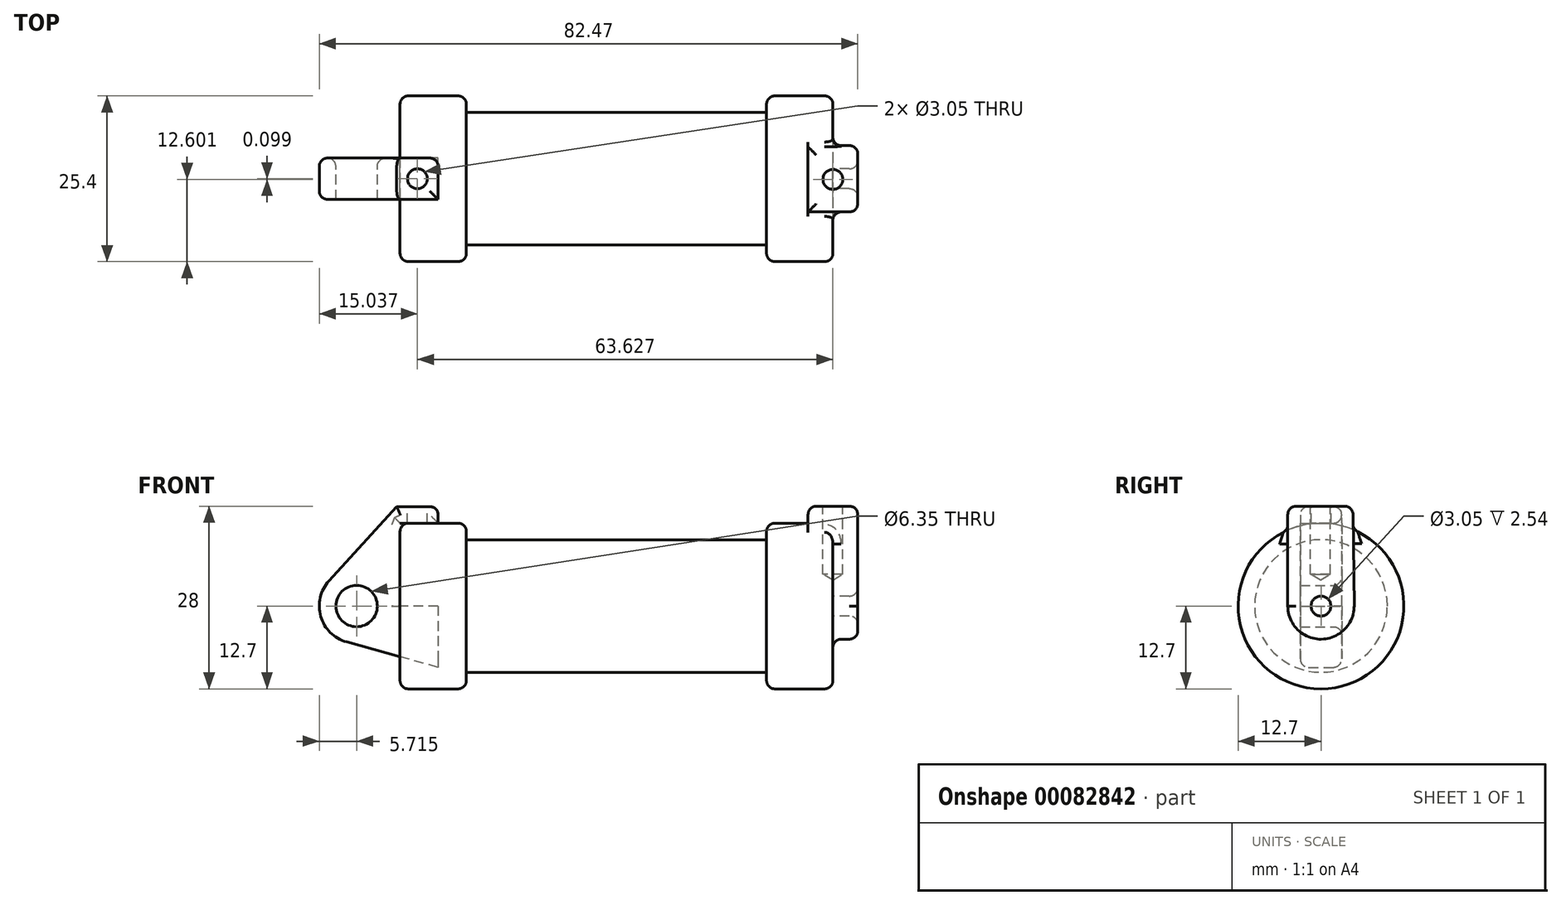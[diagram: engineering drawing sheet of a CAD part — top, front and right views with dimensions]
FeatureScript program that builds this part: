
annotation { "Feature Type Name" : "Feature", "Feature Type Description" : "" }
export const myFeature = defineFeature(function(context is Context, id is Id, definition is map)
    precondition{}
    {
        {
            var Q0;
            Q0=qCreatedBy(makeId("Front.planeOp"),FACE);
            var sketch = newSketch(context, id + "F0", { "sketchPlane" : qUnion([Q0])});
            skLineSegment(sketch, "E0", {"start": v(0, 0) * mm, "end": v(0, 12.7) * mm});
            skLineSegment(sketch, "E1", {"start": v(0, 12.7) * mm, "end": v(10.16, 12.7) * mm});
            skLineSegment(sketch, "E2", {"start": v(10.16, 12.7) * mm, "end": v(10.16, 10.16) * mm});
            skLineSegment(sketch, "E3", {"start": v(10.16, 10.16) * mm, "end": v(56.13, 10.16) * mm});
            skLineSegment(sketch, "E4", {"start": v(56.13, 10.16) * mm, "end": v(56.13, 12.7) * mm});
            skLineSegment(sketch, "E5", {"start": v(56.13, 12.7) * mm, "end": v(66.3, 12.7) * mm});
            skLineSegment(sketch, "E6", {"start": v(66.3, 12.7) * mm, "end": v(66.3, 0) * mm});
            skLineSegment(sketch, "E7", {"start": v(66.3, 0) * mm, "end": v(0, 0) * mm});
            skLineSegment(sketch, "E8", {"start": v(5.84, 15.24) * mm, "end": v(-0.5, 15.24) * mm});
            skLineSegment(sketch, "E9", {"start": v(-0.5, 15.24) * mm, "end": v(-10.88, 3.85) * mm});
            skLineSegment(sketch, "E10", {"start": v(0, 0) * mm, "end": v(-6.65, 0) * mm});
            skCircle(sketch, "E11", {"center": v(-6.65, 0) * mm, "radius": 5.72 * mm});
            skCircle(sketch, "E12", {"center": v(-6.65, 0) * mm, "radius": 3.18 * mm});
            skLineSegment(sketch, "E13", {"start": v(5.84, 15.24) * mm, "end": v(5.84, -9.4) * mm});
            skLineSegment(sketch, "E14", {"start": v(5.84, -9.4) * mm, "end": v(-8.18, -5.5) * mm});
            skSolve(sketch);
        }
        {
            var Q0;
            {var subQ0=sQuery(id+"F0.wireOp",EDGE,"E2");Q0=makeQuery(id+"F0.imprint","IMPRINT",FACE,{"disambiguationData":[TD([[makeQuery(id+"F0.imprint","IMPRINT",EDGE,{"derivedFrom":subQ0}),-1.0]])]});}
            var Q1;
            {var subQ0=sQuery(id+"F0.wireOp",EDGE,"E0");Q1=makeQuery(id+"F0.imprint","IMPRINT",FACE,{"disambiguationData":[TD([[makeQuery(id+"F0.imprint","IMPRINT",EDGE,{"derivedFrom":subQ0}),-1.0]])]});}
            var Q2;
            Q2=sQuery(id+"F0.wireOp",EDGE,"E7");
            revolve(context, id + "F1", {"entities" : qUnion([Q0, Q1]), "axis" : qUnion([Q2]), "revolveType" : RevolveType.FULL});
        }
        {
            var Q0;
            {var subQ3=sQuery(id+"F0.wireOp",EDGE,"E0");Q0=makeQuery(id+"F0.imprint","IMPRINT",FACE,{"disambiguationData":[TD([[makeQuery(id+"F0.imprint","IMPRINT",EDGE,{"derivedFrom":subQ3}),1.0]])]});}
            var Q1;
            {var subQ0=sQuery(id+"F0.wireOp",EDGE,"E14");Q1=makeQuery(id+"F0.imprint","IMPRINT",FACE,{"disambiguationData":[TD([[makeQuery(id+"F0.imprint","IMPRINT",EDGE,{"derivedFrom":subQ0}),-1.0]])]});}
            var Q2;
            {var subQ4=sQuery(id+"F0.wireOp",EDGE,"E12");Q2=makeQuery(id+"F0.imprint","IMPRINT",FACE,{"disambiguationData":[TD([[makeQuery(id+"F0.imprint","IMPRINT",EDGE,{"derivedFrom":subQ4}),-1.0]])]});}
            extrude(context, id + "F2", {"entities" : qUnion([Q0, Q1, Q2]), "endBound" : BoundingType.SYMMETRIC, "depth" : 6.35 * mm});
        }
        {
            var Q0;
            Q0=makeQuery(id+"F1.opRevolve","SWEPT_FACE",FACE,{"disambiguationData":[OSD([sQuery(id+"F0.wireOp",EDGE,"E6")])]});
            var sketch = newSketch(context, id + "F3", { "sketchPlane" : qUnion([Q0])});
            skCircle(sketch, "E15", {"center": v(0, 0) * mm, "radius": 1.52 * mm});
            skCircle(sketch, "E16", {"center": v(0, 0) * mm, "radius": 5.08 * mm});
            skLineSegment(sketch, "E17", {"start": v(-5.08, -0.04) * mm, "end": v(-5.08, 15.3) * mm});
            skLineSegment(sketch, "E18", {"start": v(-5.08, 15.3) * mm, "end": v(4.88, 15.3) * mm});
            skLineSegment(sketch, "E19", {"start": v(4.88, 15.3) * mm, "end": v(5.08, 0.07) * mm});
            skSolve(sketch);
        }
        {
            var Q0;
            {var subQ0=sQuery(id+"F3.wireOp",EDGE,"E19");var subQ1=sQuery(id+"F3.wireOp",EDGE,"E16");var subQ2=makeQuery(id+"F3.imprint","INTERSECT",VERTEX,{"derivedFrom":[subQ1,subQ0]});Q0=makeQuery(id+"F3.imprint","IMPRINT",FACE,{"disambiguationData":[TD([[makeQuery(id+"F3.imprint","IMPRINT",EDGE,{"disambiguationData":[TD([[subQ2,-1.0]])],"derivedFrom":subQ1}),-1.0]])]});}
            var Q1;
            {var subQ0=sQuery(id+"F3.wireOp",EDGE,"E18");Q1=makeQuery(id+"F3.imprint","IMPRINT",FACE,{"disambiguationData":[TD([[makeQuery(id+"F3.imprint","IMPRINT",EDGE,{"derivedFrom":subQ0}),-1.0]])]});}
            var Q2;
            Q2=makeQuery(id+"F3.imprint","IMPRINT",FACE,{"disambiguationData":[TD([[makeQuery(id+"F3.imprint","IMPRINT",EDGE,{"derivedFrom":sQuery(id+"F3.wireOp",EDGE,"E15")}),-1.0]])]});
            extrude(context, id + "F4", {"entities" : qUnion([Q0, Q1, Q2]), "operationType" : NewBodyOperationType.ADD, "endBound" : BoundingType.SYMMETRIC, "depth" : 7.62 * mm});
        }
        {
            var Q0;
            Q0=makeQuery(id+"F2.opExtrude","SWEPT_FACE",FACE,{"disambiguationData":[OSD([sQuery(id+"F0.wireOp",EDGE,"E8")])]});
            var sketch = newSketch(context, id + "F5", { "sketchPlane" : qUnion([Q0])});
            skLineSegment(sketch, "E20", {"start": v(-0.5, 3.18) * mm, "end": v(5.84, -3.18) * mm, "construction": true});
            skLineSegment(sketch, "E21", {"start": v(5.84, 3.18) * mm, "end": v(-0.5, -3.18) * mm, "construction": true});
            skCircle(sketch, "E22", {"center": v(2.67, 0) * mm, "radius": 1.52 * mm});
            skSolve(sketch);
        }
        {
            var Q0;
            Q0=makeQuery(id+"F4.opExtrude","SWEPT_FACE",FACE,{"disambiguationData":[OSD([sQuery(id+"F3.wireOp",EDGE,"E18")])]});
            var sketch = newSketch(context, id + "F6", { "sketchPlane" : qUnion([Q0])});
            skLineSegment(sketch, "E23", {"start": v(62.48, 4.88) * mm, "end": v(70.1, -5.08) * mm, "construction": true});
            skLineSegment(sketch, "E24", {"start": v(70.1, 4.88) * mm, "end": v(62.48, -5.08) * mm, "construction": true});
            skCircle(sketch, "E25", {"center": v(66.3, -0.1) * mm, "radius": 1.52 * mm});
            skSolve(sketch);
        }
        {
            var Q0;
            Q0=makeQuery(id+"F1.opRevolve","SWEPT_EDGE",EDGE,{"disambiguationData":[OSD([sQuery(id+"F0.wireOp",EDGE,"E1"),sQuery(id+"F0.wireOp",EDGE,"E2")])]});
            var Q1;
            Q1=makeQuery(id+"F1.opRevolve","SWEPT_EDGE",EDGE,{"disambiguationData":[OSD([sQuery(id+"F0.wireOp",EDGE,"E0"),sQuery(id+"F0.wireOp",EDGE,"E1")])]});
            fillet(context, id + "F7", {"entities" : qUnion([Q0, Q1]), "radius" : 1.27 * mm, "tangentPropagation" : true, "allowEdgeOverflow" : false});
        }
        {
            var Q0;
            Q0=makeQuery(id+"F1.opRevolve","SWEPT_EDGE",EDGE,{"disambiguationData":[OSD([sQuery(id+"F0.wireOp",EDGE,"E4"),sQuery(id+"F0.wireOp",EDGE,"E5")])]});
            var Q1;
            Q1=makeQuery(id+"F1.opRevolve","SWEPT_EDGE",EDGE,{"disambiguationData":[OSD([sQuery(id+"F0.wireOp",EDGE,"E5"),sQuery(id+"F0.wireOp",EDGE,"E6")])]});
            fillet(context, id + "F8", {"entities" : qUnion([Q0, Q1]), "radius" : 1.27 * mm, "tangentPropagation" : true, "allowEdgeOverflow" : false});
        }
        {
            var Q0;
            Q0=makeQuery(id+"F4.opExtrude","CAP_FACE",FACE,{"disambiguationData":[OSD([sQuery(id+"F3.wireOp",EDGE,"E15"),sQuery(id+"F3.wireOp",EDGE,"E16"),sQuery(id+"F3.wireOp",EDGE,"E17"),sQuery(id+"F3.wireOp",EDGE,"E18"),sQuery(id+"F3.wireOp",EDGE,"E19")])],"isStart":false});
            var Q1;
            Q1=makeQuery(id+"F4.opExtrude","SWEPT_EDGE",EDGE,{"disambiguationData":[OSD([sQuery(id+"F3.wireOp",EDGE,"E17"),sQuery(id+"F3.wireOp",EDGE,"E18")])]});
            var Q2;
            Q2=makeQuery(id+"F4.boolean.opBoolean","INTERSECT",EDGE,{"derivedFrom":[makeQuery(id+"F1.opRevolve","SWEPT_FACE",FACE,{"disambiguationData":[OSD([sQuery(id+"F0.wireOp",EDGE,"E6")])]}),makeQuery(id+"F4.opExtrude","SWEPT_FACE",FACE,{"disambiguationData":[OSD([sQuery(id+"F3.wireOp",EDGE,"E17")])]})]});
            var Q3;
            Q3=makeQuery(id+"F4.boolean.opBoolean","INTERSECT",EDGE,{"derivedFrom":[makeQuery(id+"F1.opRevolve","SWEPT_FACE",FACE,{"disambiguationData":[OSD([sQuery(id+"F0.wireOp",EDGE,"E5")])]}),makeQuery(id+"F4.opExtrude","SWEPT_FACE",FACE,{"disambiguationData":[OSD([sQuery(id+"F3.wireOp",EDGE,"E17")])]})]});
            var Q4;
            Q4=makeQuery(id+"F8.opFillet","BLEND_EDGE",EDGE,{"blendedFrom":[makeQuery(id+"F1.opRevolve","SWEPT_EDGE",EDGE,{"disambiguationData":[OSD([sQuery(id+"F0.wireOp",EDGE,"E5"),sQuery(id+"F0.wireOp",EDGE,"E6")])]}),makeQuery(id+"F4.opExtrude","SWEPT_FACE",FACE,{"disambiguationData":[OSD([sQuery(id+"F3.wireOp",EDGE,"E17")])]})],"blendedInto":[makeQuery(id+"F4.opExtrude","SWEPT_FACE",FACE,{"disambiguationData":[OSD([sQuery(id+"F3.wireOp",EDGE,"E17")])]})]});
            var Q5;
            Q5=makeQuery(id+"F4.boolean.opBoolean","INTERSECT",EDGE,{"derivedFrom":[makeQuery(id+"F1.opRevolve","SWEPT_FACE",FACE,{"disambiguationData":[OSD([sQuery(id+"F0.wireOp",EDGE,"E6")])]}),makeQuery(id+"F4.opExtrude","SWEPT_FACE",FACE,{"disambiguationData":[OSD([sQuery(id+"F3.wireOp",EDGE,"E16")])]})]});
            var Q6;
            Q6=makeQuery(id+"F4.opExtrude","CAP_EDGE",EDGE,{"disambiguationData":[OSD([sQuery(id+"F3.wireOp",EDGE,"E16")])],"isStart":false});
            var Q7;
            Q7=makeQuery(id+"F4.opExtrude","CAP_EDGE",EDGE,{"disambiguationData":[OSD([sQuery(id+"F3.wireOp",EDGE,"E17")])],"isStart":false});
            var Q8;
            {var subQ0=sQuery(id+"F0.wireOp",EDGE,"E5");var subQ1=sQuery(id+"F0.wireOp",EDGE,"E6");Q8=makeQuery(id+"F8.opFillet","BLEND_EDGE",EDGE,{"blendedFrom":[makeQuery(id+"F1.opRevolve","SWEPT_EDGE",EDGE,{"disambiguationData":[OSD([subQ0,subQ1])]}),makeQuery(id+"F4.boolean.opBoolean","SPLIT",FACE,{"disambiguationData":[TD([makeQuery(id+"F1.opRevolve","SWEPT_FACE",FACE,{"disambiguationData":[OSD([subQ0])]})])],"derivedFrom":makeQuery(id+"F1.opRevolve","SWEPT_FACE",FACE,{"disambiguationData":[OSD([subQ1])]})})],"blendedInto":[makeQuery(id+"F4.boolean.opBoolean","SPLIT",FACE,{"disambiguationData":[TD([makeQuery(id+"F1.opRevolve","SWEPT_FACE",FACE,{"disambiguationData":[OSD([subQ0])]})])],"derivedFrom":makeQuery(id+"F1.opRevolve","SWEPT_FACE",FACE,{"disambiguationData":[OSD([subQ1])]})})]});}
            var Q9;
            Q9=makeQuery(id+"F4.opExtrude","CAP_EDGE",EDGE,{"disambiguationData":[OSD([sQuery(id+"F3.wireOp",EDGE,"E18")])],"isStart":false});
            var Q10;
            Q10=makeQuery(id+"F4.opExtrude","SWEPT_EDGE",EDGE,{"disambiguationData":[OSD([sQuery(id+"F3.wireOp",EDGE,"E18"),sQuery(id+"F3.wireOp",EDGE,"E19")])]});
            var Q11;
            Q11=makeQuery(id+"F4.opExtrude","CAP_EDGE",EDGE,{"disambiguationData":[OSD([sQuery(id+"F3.wireOp",EDGE,"E18")])],"isStart":true});
            var Q12;
            Q12=makeQuery(id+"F4.opExtrude","CAP_EDGE",EDGE,{"disambiguationData":[OSD([sQuery(id+"F3.wireOp",EDGE,"E19")])],"isStart":false});
            var Q13;
            Q13=makeQuery(id+"F4.boolean.opBoolean","SPLIT",FACE,{"disambiguationData":[TD([makeQuery(id+"F1.opRevolve","SWEPT_FACE",FACE,{"disambiguationData":[OSD([sQuery(id+"F0.wireOp",EDGE,"E5")])]})])],"derivedFrom":makeQuery(id+"F1.opRevolve","SWEPT_FACE",FACE,{"disambiguationData":[OSD([sQuery(id+"F0.wireOp",EDGE,"E6")])]})});
            var Q14;
            Q14=makeQuery(id+"F8.opFillet","BLEND_EDGE",EDGE,{"blendedFrom":[makeQuery(id+"F1.opRevolve","SWEPT_EDGE",EDGE,{"disambiguationData":[OSD([sQuery(id+"F0.wireOp",EDGE,"E5"),sQuery(id+"F0.wireOp",EDGE,"E6")])]}),makeQuery(id+"F4.opExtrude","SWEPT_FACE",FACE,{"disambiguationData":[OSD([sQuery(id+"F3.wireOp",EDGE,"E19")])]})],"blendedInto":[makeQuery(id+"F4.opExtrude","SWEPT_FACE",FACE,{"disambiguationData":[OSD([sQuery(id+"F3.wireOp",EDGE,"E19")])]})]});
            var Q15;
            Q15=makeQuery(id+"F4.boolean.opBoolean","INTERSECT",EDGE,{"derivedFrom":[makeQuery(id+"F1.opRevolve","SWEPT_FACE",FACE,{"disambiguationData":[OSD([sQuery(id+"F0.wireOp",EDGE,"E5")])]}),makeQuery(id+"F4.opExtrude","SWEPT_FACE",FACE,{"disambiguationData":[OSD([sQuery(id+"F3.wireOp",EDGE,"E19")])]})]});
            fillet(context, id + "F9", {"entities" : qUnion([Q0, Q1, Q2, Q3, Q4, Q5, Q6, Q7, Q8, Q9, Q10, Q11, Q12, Q13, Q14, Q15]), "radius" : 1.27 * mm, "tangentPropagation" : true, "allowEdgeOverflow" : false});
        }
        {
            var Q0;
            Q0=makeQuery(id+"F2.opExtrude","CAP_EDGE",EDGE,{"disambiguationData":[OSD([sQuery(id+"F0.wireOp",EDGE,"E14")])],"isStart":true});
            var Q1;
            Q1=makeQuery(id+"F2.opExtrude","CAP_EDGE",EDGE,{"disambiguationData":[OSD([sQuery(id+"F0.wireOp",EDGE,"E14")])],"isStart":false});
            var Q2;
            Q2=makeQuery(id+"F2.opExtrude","CAP_EDGE",EDGE,{"disambiguationData":[OSD([sQuery(id+"F0.wireOp",EDGE,"E11")])],"isStart":false});
            var Q3;
            Q3=makeQuery(id+"F2.opExtrude","CAP_EDGE",EDGE,{"disambiguationData":[OSD([sQuery(id+"F0.wireOp",EDGE,"E11")])],"isStart":true});
            var Q4;
            Q4=makeQuery(id+"F2.opExtrude","CAP_EDGE",EDGE,{"disambiguationData":[OSD([sQuery(id+"F0.wireOp",EDGE,"E9")])],"isStart":true});
            var Q5;
            Q5=makeQuery(id+"F2.opExtrude","CAP_EDGE",EDGE,{"disambiguationData":[OSD([sQuery(id+"F0.wireOp",EDGE,"E9")])],"isStart":false});
            var Q6;
            Q6=makeQuery(id+"F2.opExtrude","CAP_EDGE",EDGE,{"disambiguationData":[OSD([sQuery(id+"F0.wireOp",EDGE,"E8")])],"isStart":false});
            var Q7;
            Q7=makeQuery(id+"FPSyX7AReI34fN4_2.hole-0.boolean.opBoolean","COPY",EDGE,{"derivedFrom":makeQuery(id+"FPSyX7AReI34fN4_2.hole-0.opRevolve","SWEPT_EDGE",EDGE,{"disambiguationData":[OSD([sQuery(id+"FPSyX7AReI34fN4_2.hole-0.sketch.wireOp",EDGE,"core_line_2"),sQuery(id+"FPSyX7AReI34fN4_2.hole-0.sketch.wireOp",EDGE,"core_line_3")])]})});
            var Q8;
            Q8=makeQuery(id+"F2.opExtrude","CAP_EDGE",EDGE,{"disambiguationData":[OSD([sQuery(id+"F0.wireOp",EDGE,"E8")])],"isStart":true});
            var Q9;
            Q9=makeQuery(id+"F2.opExtrude","SWEPT_EDGE",EDGE,{"disambiguationData":[OSD([sQuery(id+"F0.wireOp",EDGE,"E8"),sQuery(id+"F0.wireOp",EDGE,"E13")])]});
            var Q10;
            {var subQ0=sQuery(id+"F0.wireOp",EDGE,"E13");Q10=makeQuery(id+"F2.opExtrude","CAP_EDGE",EDGE,{"disambiguationData":[OSD([subQ0]),TDD([makeQuery(id+"F0.imprint","IMPRINT",EDGE,{"disambiguationData":[TD([[makeQuery(id+"F0.imprint","INTERSECT",VERTEX,{"derivedFrom":[sQuery(id+"F0.wireOp",EDGE,"E8"),subQ0]}),-1.0]])],"derivedFrom":subQ0})])],"isStart":true});}
            var Q11;
            Q11=makeQuery(id+"F2.opExtrude","CAP_EDGE",EDGE,{"disambiguationData":[OSD([sQuery(id+"F0.wireOp",EDGE,"E1")])],"isStart":true});
            var Q12;
            Q12=makeQuery(id+"F2.opExtrude","CAP_EDGE",EDGE,{"disambiguationData":[OSD([sQuery(id+"F0.wireOp",EDGE,"E0")])],"isStart":true});
            var Q13;
            Q13=makeQuery(id+"F2.opExtrude","CAP_EDGE",EDGE,{"disambiguationData":[OSD([sQuery(id+"F0.wireOp",EDGE,"E12")])],"isStart":true});
            fillet(context, id + "F10", {"entities" : qUnion([Q0, Q1, Q2, Q3, Q4, Q5, Q6, Q7, Q8, Q9, Q10, Q11, Q12, Q13]), "radius" : 1.27 * mm, "tangentPropagation" : true, "allowEdgeOverflow" : false});
        }
        {
            var Q0;
            Q0=sQuery(id+"F6.wireOp",VERTEX,"E25.center");
            var Q1;
            Q1=makeQuery(id+"F1.opRevolve","SWEPT_BODY",BODY,{"disambiguationData":[OSD([sQuery(id+"F0.wireOp",EDGE,"E0"),sQuery(id+"F0.wireOp",EDGE,"E1"),sQuery(id+"F0.wireOp",EDGE,"E2"),sQuery(id+"F0.wireOp",EDGE,"E3"),sQuery(id+"F0.wireOp",EDGE,"E4"),sQuery(id+"F0.wireOp",EDGE,"E5"),sQuery(id+"F0.wireOp",EDGE,"E6"),sQuery(id+"F0.wireOp",EDGE,"E7")])]});
            hole(context, id + "F11", {"style" : HoleStyle.SIMPLE, "endStyle" : HoleEndStyle.BLIND, "holeDiameter" : 3.05 * mm, "holeDepth" : 10.4 * mm, "locations" : qUnion([Q0]), "scope" : qUnion([Q1])});
        }
        {
            var Q0;
            Q0=sQuery(id+"F5.wireOp",VERTEX,"E22.center");
            var Q1;
            Q1=makeQuery(id+"F2.opExtrude","SWEPT_BODY",BODY,{"disambiguationData":[OSD([sQuery(id+"F0.wireOp",EDGE,"E0"),sQuery(id+"F0.wireOp",EDGE,"E1"),sQuery(id+"F0.wireOp",EDGE,"E7"),sQuery(id+"F0.wireOp",EDGE,"E8"),sQuery(id+"F0.wireOp",EDGE,"E9"),sQuery(id+"F0.wireOp",EDGE,"E11"),sQuery(id+"F0.wireOp",EDGE,"E12"),sQuery(id+"F0.wireOp",EDGE,"E13"),sQuery(id+"F0.wireOp",EDGE,"E14")])]});
            hole(context, id + "F12", {"style" : HoleStyle.SIMPLE, "endStyle" : HoleEndStyle.BLIND, "holeDiameter" : 3.05 * mm, "holeDepth" : 10.4 * mm, "locations" : qUnion([Q0]), "scope" : qUnion([Q1])});
        }
    });
